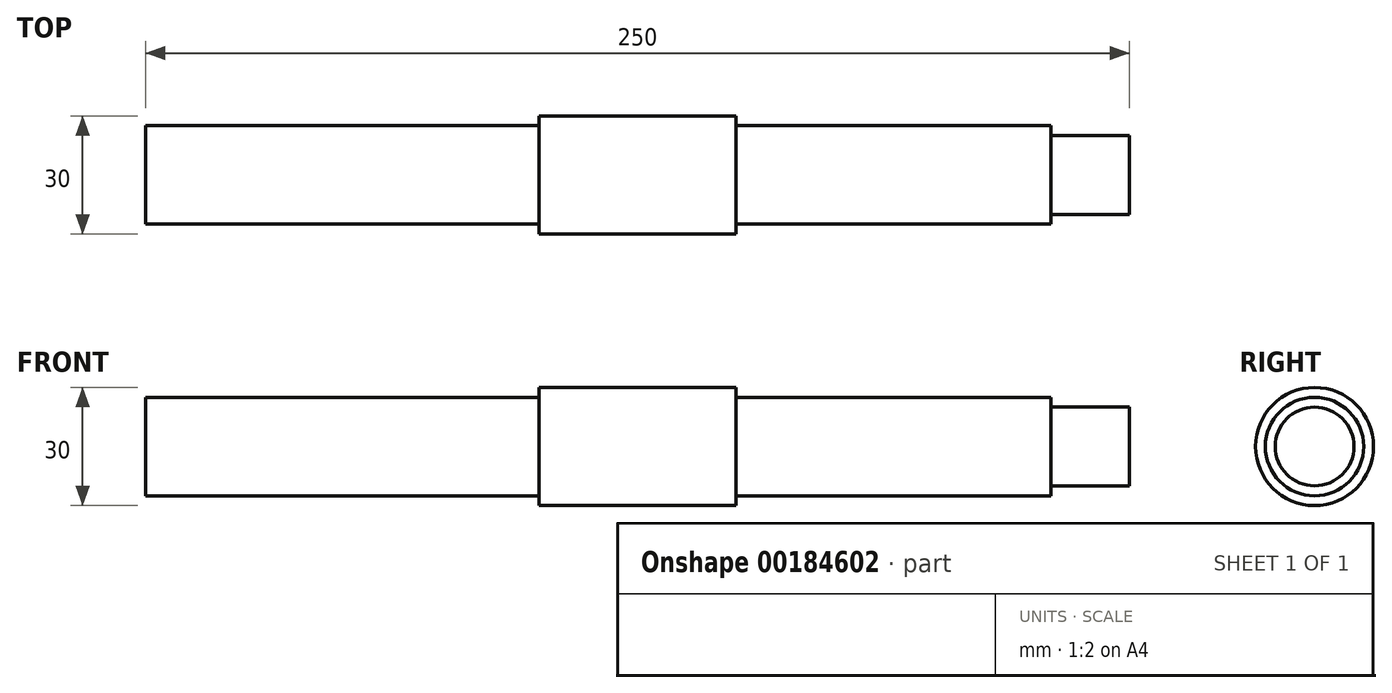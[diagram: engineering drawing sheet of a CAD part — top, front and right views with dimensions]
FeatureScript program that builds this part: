
annotation { "Feature Type Name" : "Feature", "Feature Type Description" : "" }
export const myFeature = defineFeature(function(context is Context, id is Id, definition is map)
    precondition{}
    {
        {
            var Q0;
            Q0=qCreatedBy(makeId("Front.planeOp"),FACE);
            var sketch = newSketch(context, id + "F0", { "sketchPlane" : qUnion([Q0])});
            skLineSegment(sketch, "E0", {"start": v(-64.03, 0) * mm, "end": v(-64.03, -12.5) * mm});
            skLineSegment(sketch, "E1", {"start": v(35.97, -12.5) * mm, "end": v(35.97, -15) * mm});
            skLineSegment(sketch, "E2", {"start": v(35.97, -15) * mm, "end": v(85.97, -15) * mm});
            skLineSegment(sketch, "E3", {"start": v(85.97, -15) * mm, "end": v(85.97, -12.5) * mm});
            skLineSegment(sketch, "E4", {"start": v(85.97, -12.5) * mm, "end": v(165.97, -12.5) * mm});
            skLineSegment(sketch, "E5", {"start": v(165.97, -12.5) * mm, "end": v(165.97, -10) * mm});
            skLineSegment(sketch, "E6", {"start": v(165.97, -10) * mm, "end": v(185.97, -10) * mm});
            skLineSegment(sketch, "E7", {"start": v(185.97, -10) * mm, "end": v(185.97, 0) * mm});
            skLineSegment(sketch, "E8", {"start": v(185.97, 0) * mm, "end": v(-64.03, 0) * mm});
            skLineSegment(sketch, "E9", {"start": v(-64.03, -12.5) * mm, "end": v(35.97, -12.5) * mm});
            skSolve(sketch);
        }
        {
            var Q0;
            Q0=makeQuery(id+"F0.imprint","IMPRINT",FACE,{"disambiguationData":[TD([[makeQuery(id+"F0.imprint","IMPRINT",EDGE,{"derivedFrom":sQuery(id+"F0.wireOp",EDGE,"E0")}),1.0]])]});
            var Q1;
            Q1=sQuery(id+"F0.wireOp",EDGE,"E8");
            revolve(context, id + "F1", {"entities" : qUnion([Q0]), "axis" : qUnion([Q1]), "revolveType" : RevolveType.FULL});
        }
    });
